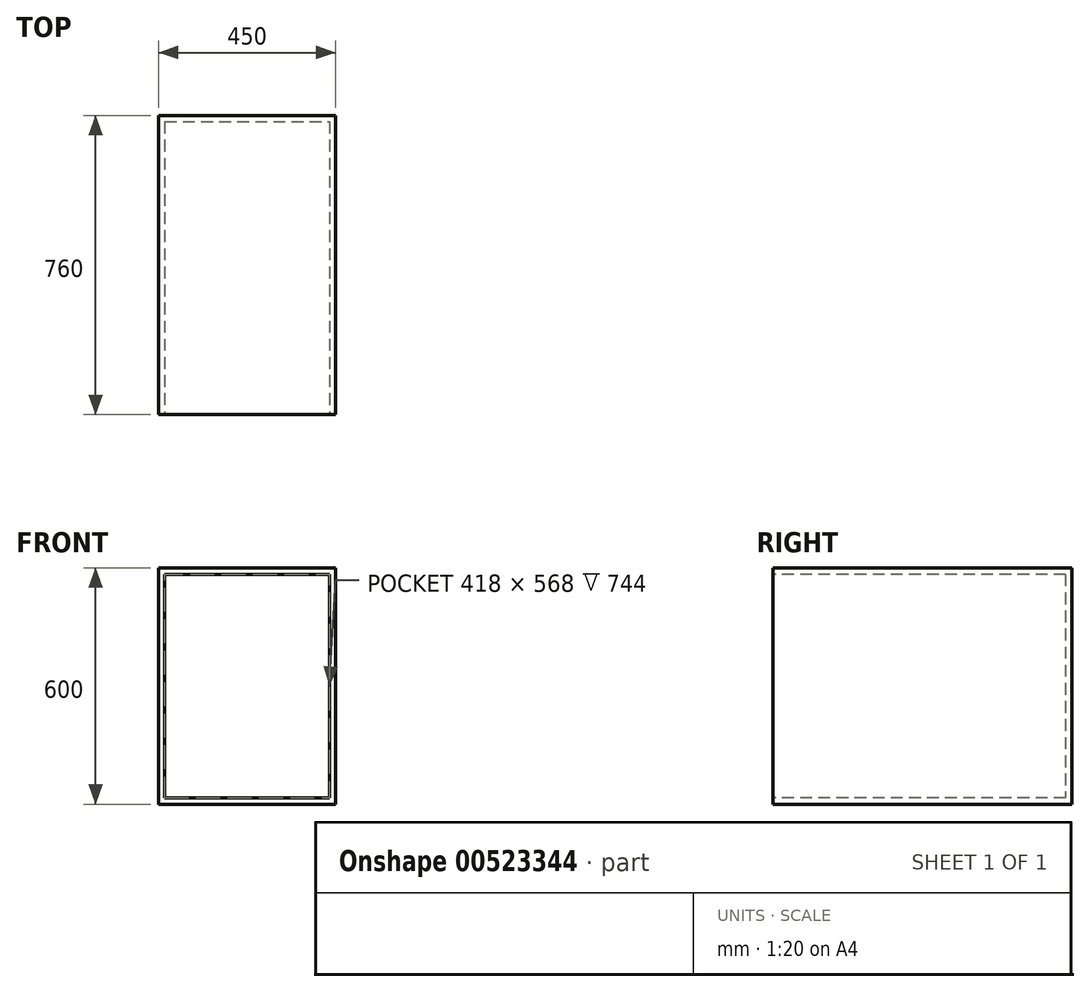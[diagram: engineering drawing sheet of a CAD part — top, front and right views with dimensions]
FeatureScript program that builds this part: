
annotation { "Feature Type Name" : "Feature", "Feature Type Description" : "" }
export const myFeature = defineFeature(function(context is Context, id is Id, definition is map)
    precondition{}
    {
        {
            var Q0;
            Q0=qCreatedBy(makeId("Front.planeOp"),FACE);
            var sketch = newSketch(context, id + "F0", { "sketchPlane" : qUnion([Q0])});
            skLineSegment(sketch, "E0.bottom", {"start": v(-225, 300) * mm, "end": v(225, 300) * mm});
            skLineSegment(sketch, "E0.top", {"start": v(-225, -300) * mm, "end": v(225, -300) * mm});
            skLineSegment(sketch, "E0.left", {"start": v(-225, 300) * mm, "end": v(-225, -300) * mm});
            skLineSegment(sketch, "E0.right", {"start": v(225, 300) * mm, "end": v(225, -300) * mm});
            skPoint(sketch, "E0.middle", {"position": v(0, 0) * mm});
            skSolve(sketch);
        }
        {
            var Q0;
            Q0 = qSketchRegion(id + "F0", true);
            extrude(context, id + "F1", {"entities" : qUnion([Q0]), "depth" : 760 * mm, "offsetDistance" : 25 * mm});
        }
        {
            var Q0;
            Q0=makeQuery(id+"F1.opExtrude","CAP_FACE",FACE,{"disambiguationData":[OSD([sQuery(id+"F0.wireOp",EDGE,"E0.bottom"),sQuery(id+"F0.wireOp",EDGE,"E0.top"),sQuery(id+"F0.wireOp",EDGE,"E0.left"),sQuery(id+"F0.wireOp",EDGE,"E0.right")])],"isStart":false});
            var sketch = newSketch(context, id + "F2", { "sketchPlane" : qUnion([Q0])});
            skLineSegment(sketch, "E1.bottom", {"start": v(-209, 284) * mm, "end": v(209, 284) * mm});
            skLineSegment(sketch, "E1.top", {"start": v(-209, -284) * mm, "end": v(209, -284) * mm});
            skLineSegment(sketch, "E1.left", {"start": v(-209, 284) * mm, "end": v(-209, -284) * mm});
            skLineSegment(sketch, "E1.right", {"start": v(209, 284) * mm, "end": v(209, -284) * mm});
            skPoint(sketch, "E1.middle", {"position": v(0, 0) * mm});
            skSolve(sketch);
        }
        {
            var Q0;
            Q0 = qSketchRegion(id + "F2", true);
            extrude(context, id + "F3", {"entities" : qUnion([Q0]), "operationType" : NewBodyOperationType.REMOVE, "oppositeDirection" : true, "depth" : 744 * mm, "offsetDistance" : 25 * mm});
        }
    });
